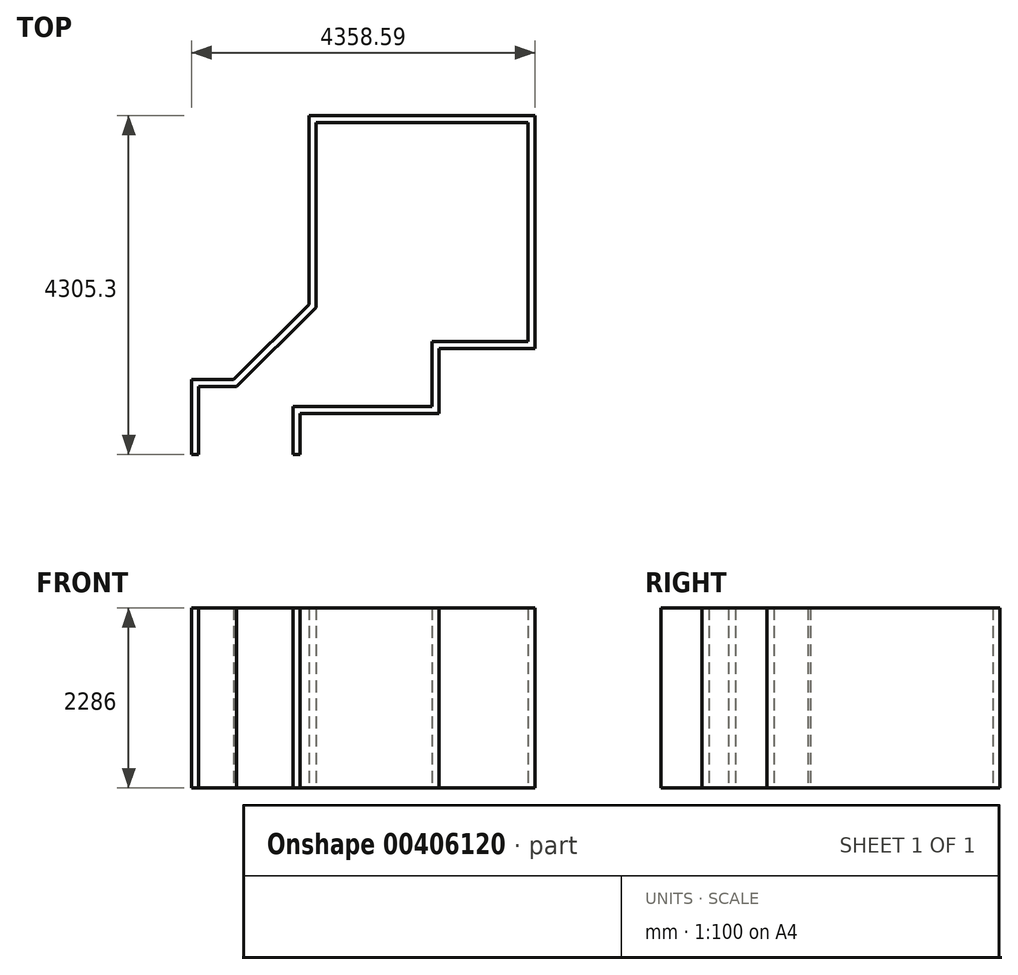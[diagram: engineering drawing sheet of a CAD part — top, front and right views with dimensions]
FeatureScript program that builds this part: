
annotation { "Feature Type Name" : "Feature", "Feature Type Description" : "" }
export const myFeature = defineFeature(function(context is Context, id is Id, definition is map)
    precondition{}
    {
        {
            var Q0;
            Q0=qCreatedBy(makeId("Top.planeOp"),FACE);
            var sketch = newSketch(context, id + "F0", { "sketchPlane" : qUnion([Q0])});
            skLineSegment(sketch, "E0", {"start": v(0, 0) * mm, "end": v(-2692.4, 0) * mm});
            skLineSegment(sketch, "E1", {"start": v(-2692.4, 0) * mm, "end": v(-2692.4, -2349.5) * mm});
            skLineSegment(sketch, "E2", {"start": v(-2692.4, -2349.5) * mm, "end": v(-3698.19, -3355.29) * mm});
            skLineSegment(sketch, "E3", {"start": v(-3698.19, -3355.29) * mm, "end": v(-4180.79, -3355.29) * mm});
            skLineSegment(sketch, "E4", {"start": v(-4180.79, -3355.29) * mm, "end": v(-4180.79, -4216.4) * mm});
            skLineSegment(sketch, "E5", {"start": v(0, 0) * mm, "end": v(0, -2781.3) * mm});
            skLineSegment(sketch, "E6", {"start": v(0, -2781.3) * mm, "end": v(-1219.2, -2781.3) * mm});
            skLineSegment(sketch, "E7", {"start": v(-1219.2, -2781.3) * mm, "end": v(-1219.2, -3606.8) * mm});
            skLineSegment(sketch, "E8", {"start": v(-1219.2, -3606.8) * mm, "end": v(-2984.5, -3606.8) * mm});
            skLineSegment(sketch, "E9", {"start": v(-2984.5, -3606.8) * mm, "end": v(-2984.5, -4216.4) * mm});
            skLineSegment(sketch, "E10.0", {"start": v(-4269.69, -3266.39) * mm, "end": v(-4269.69, -4216.4) * mm});
            skLineSegment(sketch, "E10.1", {"start": v(-3735.01, -3266.39) * mm, "end": v(-4269.69, -3266.39) * mm});
            skLineSegment(sketch, "E10.2", {"start": v(-2781.3, -2312.68) * mm, "end": v(-3735.01, -3266.39) * mm});
            skLineSegment(sketch, "E10.3", {"start": v(-2781.3, 88.9) * mm, "end": v(-2781.3, -2312.68) * mm});
            skLineSegment(sketch, "E10.4", {"start": v(88.9, 88.9) * mm, "end": v(-2781.3, 88.9) * mm});
            skLineSegment(sketch, "E10.5", {"start": v(88.9, 88.9) * mm, "end": v(88.9, -2870.2) * mm});
            skLineSegment(sketch, "E10.6", {"start": v(-2895.6, -3695.7) * mm, "end": v(-2895.6, -4216.4) * mm});
            skLineSegment(sketch, "E10.7", {"start": v(-1130.3, -3695.7) * mm, "end": v(-2895.6, -3695.7) * mm});
            skLineSegment(sketch, "E10.8", {"start": v(-1130.3, -2870.2) * mm, "end": v(-1130.3, -3695.7) * mm});
            skLineSegment(sketch, "E10.9", {"start": v(88.9, -2870.2) * mm, "end": v(-1130.3, -2870.2) * mm});
            skLineSegment(sketch, "E11", {"start": v(-4269.69, -4216.4) * mm, "end": v(-4180.79, -4216.4) * mm});
            skLineSegment(sketch, "E12", {"start": v(-2895.6, -4216.4) * mm, "end": v(-2984.5, -4216.4) * mm});
            skSolve(sketch);
        }
        {
            var Q0;
            Q0 = qSketchRegion(id + "F0", true);
            extrude(context, id + "F1", {"entities" : qUnion([Q0]), "depth" : 2286 * mm});
        }
    });
